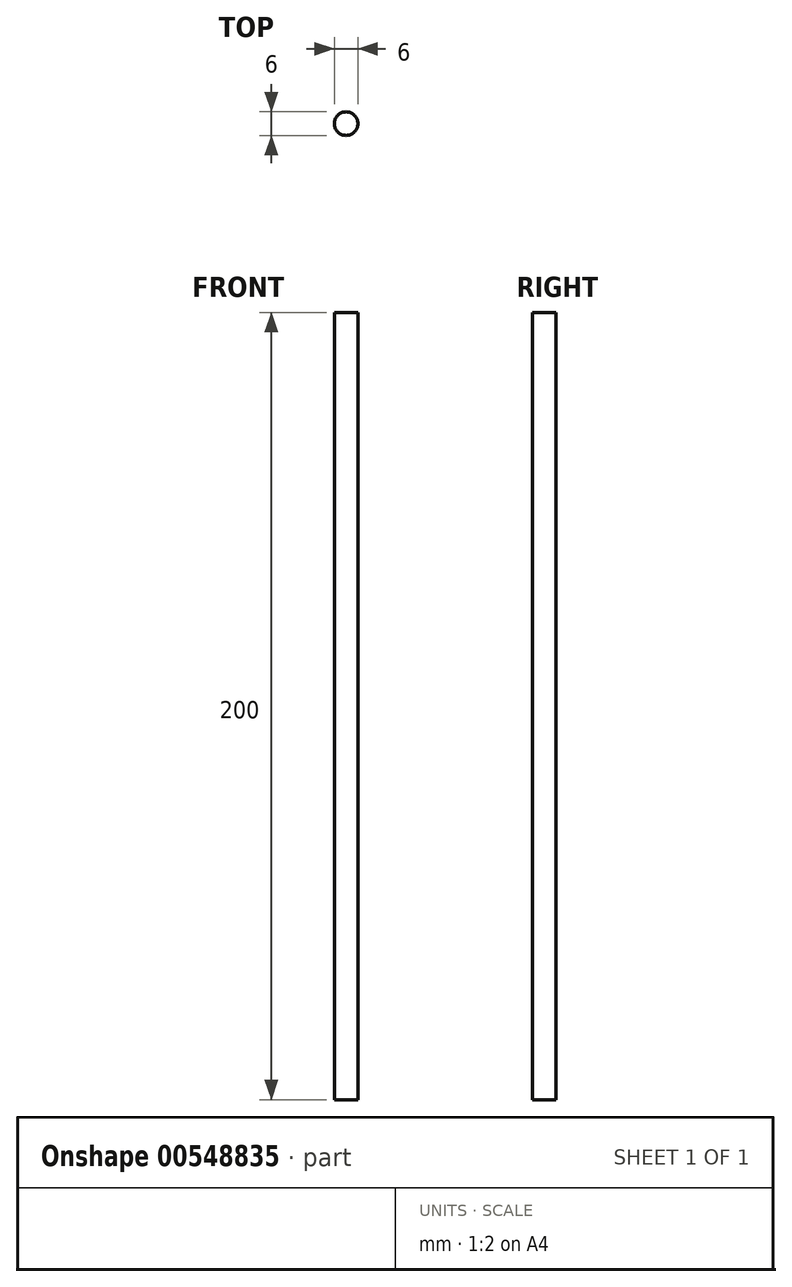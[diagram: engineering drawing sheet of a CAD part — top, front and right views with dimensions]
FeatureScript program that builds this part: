
annotation { "Feature Type Name" : "Feature", "Feature Type Description" : "" }
export const myFeature = defineFeature(function(context is Context, id is Id, definition is map)
    precondition{}
    {
        {
            var Q0;
            Q0=qCreatedBy(makeId("Top.planeOp"),FACE);
            var sketch = newSketch(context, id + "F0", { "sketchPlane" : qUnion([Q0])});
            skCircle(sketch, "E0", {"center": v(0, 0) * mm, "radius": 3 * mm});
            skSolve(sketch);
        }
        {
            var Q0;
            Q0 = qSketchRegion(id + "F0", true);
            extrude(context, id + "F1", {"entities" : qUnion([Q0]), "depth" : 200 * mm, "offsetDistance" : 25 * mm});
        }
    });
